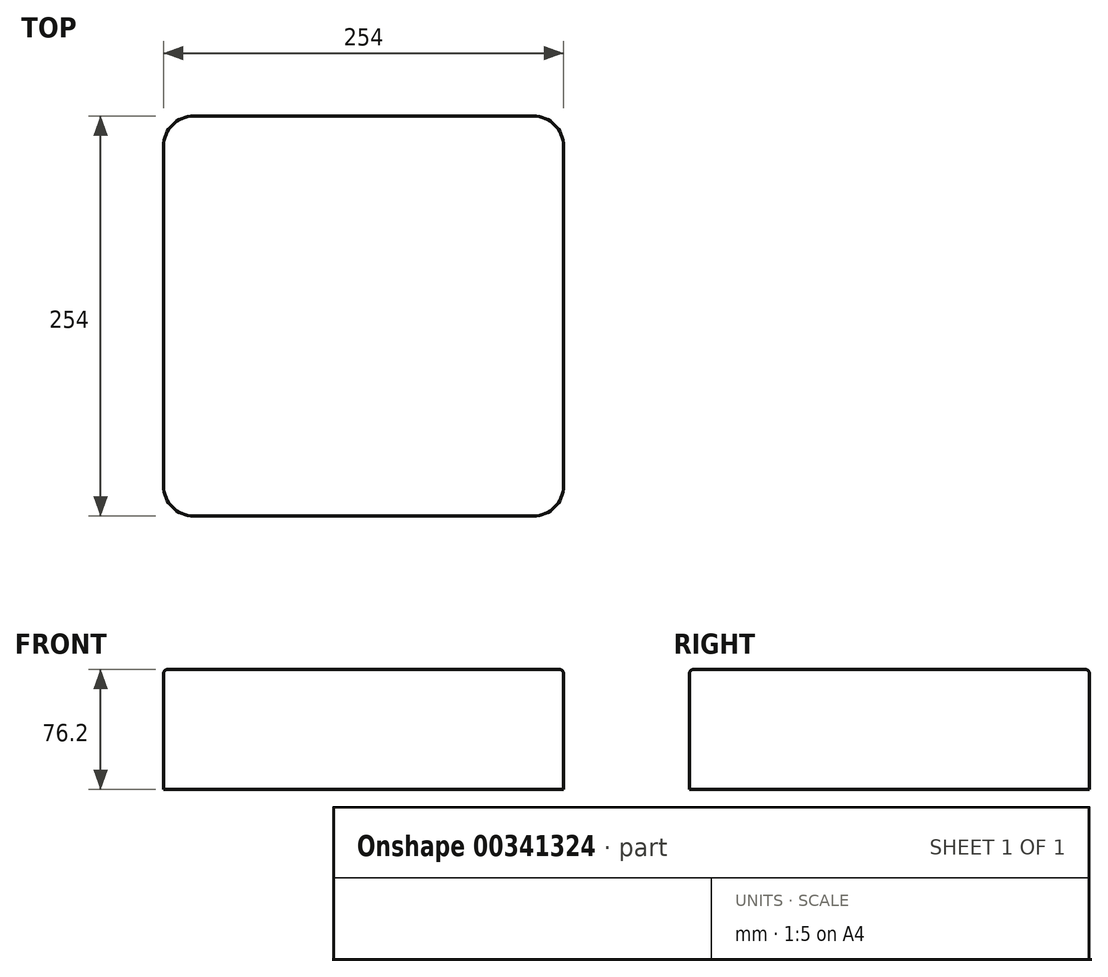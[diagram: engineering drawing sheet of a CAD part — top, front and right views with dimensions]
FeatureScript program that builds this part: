
annotation { "Feature Type Name" : "Feature", "Feature Type Description" : "" }
export const myFeature = defineFeature(function(context is Context, id is Id, definition is map)
    precondition{}
    {
        {
            var Q0;
            Q0=qCreatedBy(makeId("Top.planeOp"),FACE);
            var sketch = newSketch(context, id + "F0", { "sketchPlane" : qUnion([Q0])});
            skLineSegment(sketch, "E0.bottom", {"start": v(127, 127) * mm, "end": v(-127, 127) * mm});
            skLineSegment(sketch, "E0.top", {"start": v(127, -127) * mm, "end": v(-127, -127) * mm});
            skLineSegment(sketch, "E0.left", {"start": v(127, 127) * mm, "end": v(127, -127) * mm});
            skLineSegment(sketch, "E0.right", {"start": v(-127, 127) * mm, "end": v(-127, -127) * mm});
            skPoint(sketch, "E0.middle", {"position": v(0, 0) * mm});
            skSolve(sketch);
        }
        {
            var Q0;
            Q0 = qSketchRegion(id + "F0", true);
            extrude(context, id + "F1", {"entities" : qUnion([Q0]), "depth" : 76.2 * mm});
        }
        {
            var Q0;
            Q0=makeQuery(id+"F1.opExtrude","SWEPT_EDGE",EDGE,{"disambiguationData":[OSD([sQuery(id+"F0.wireOp",EDGE,"E0.top"),sQuery(id+"F0.wireOp",EDGE,"E0.left")])]});
            var Q1;
            Q1=makeQuery(id+"F1.opExtrude","SWEPT_EDGE",EDGE,{"disambiguationData":[OSD([sQuery(id+"F0.wireOp",EDGE,"E0.bottom"),sQuery(id+"F0.wireOp",EDGE,"E0.left")])]});
            var Q2;
            Q2=makeQuery(id+"F1.opExtrude","SWEPT_EDGE",EDGE,{"disambiguationData":[OSD([sQuery(id+"F0.wireOp",EDGE,"E0.bottom"),sQuery(id+"F0.wireOp",EDGE,"E0.right")])]});
            var Q3;
            Q3=makeQuery(id+"F1.opExtrude","SWEPT_EDGE",EDGE,{"disambiguationData":[OSD([sQuery(id+"F0.wireOp",EDGE,"E0.top"),sQuery(id+"F0.wireOp",EDGE,"E0.right")])]});
            fillet(context, id + "F2", {"entities" : qUnion([Q0, Q1, Q2, Q3]), "radius" : 19.05 * mm, "tangentPropagation" : true, "allowEdgeOverflow" : false});
        }
        {
            var Q0;
            Q0=makeQuery(id+"F1.opExtrude","CAP_EDGE",EDGE,{"disambiguationData":[OSD([sQuery(id+"F0.wireOp",EDGE,"E0.left")])],"isStart":false});
            fillet(context, id + "F3", {"entities" : qUnion([Q0]), "radius" : 2.54 * mm, "tangentPropagation" : true, "allowEdgeOverflow" : false});
        }
    });
